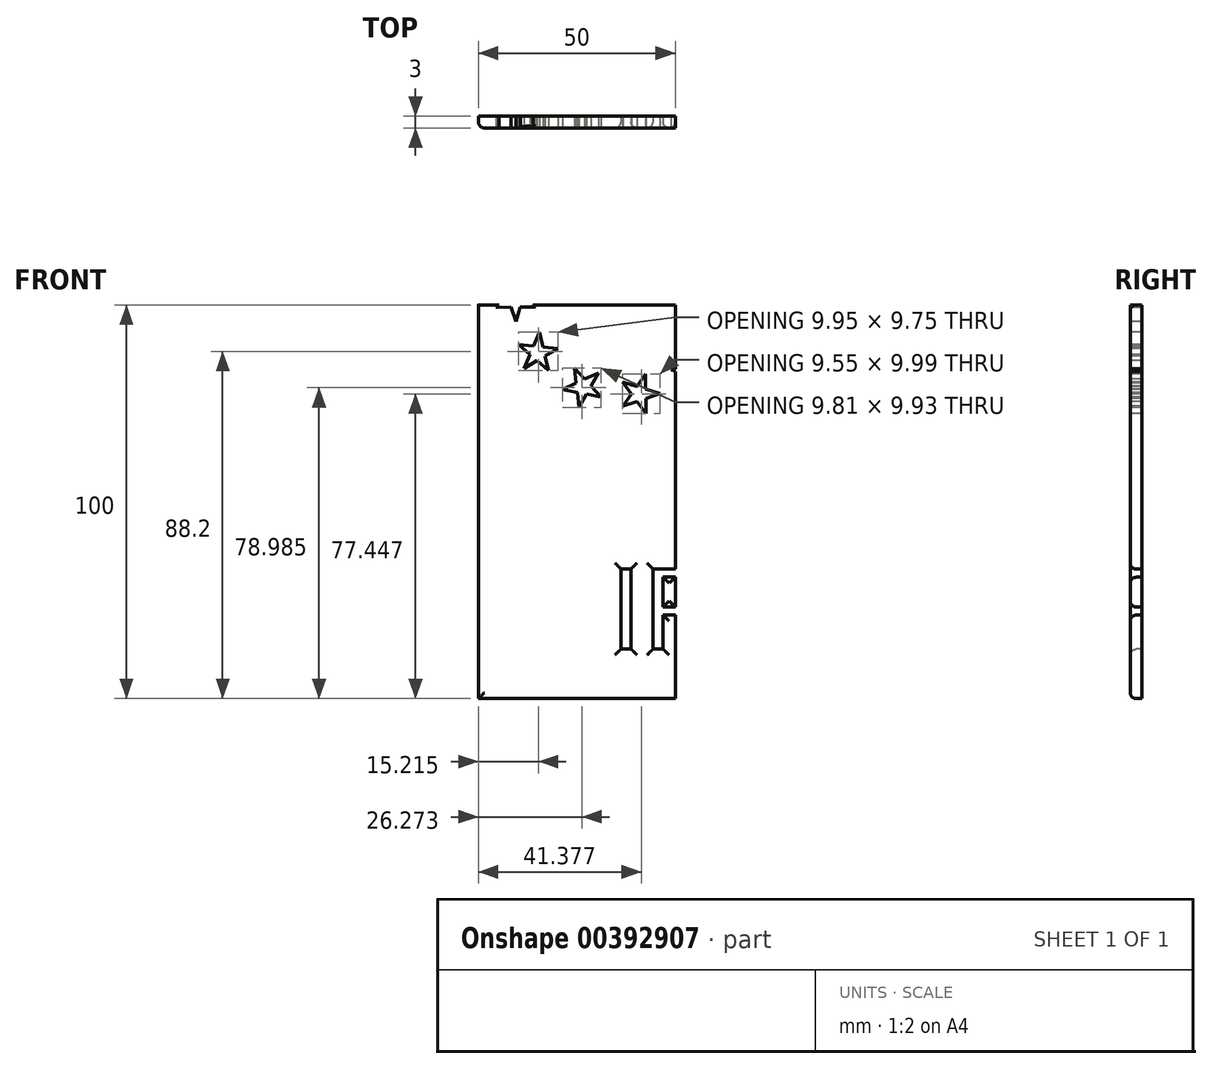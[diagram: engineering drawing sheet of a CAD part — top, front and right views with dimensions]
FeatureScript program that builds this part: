
annotation { "Feature Type Name" : "Feature", "Feature Type Description" : "" }
export const myFeature = defineFeature(function(context is Context, id is Id, definition is map)
    precondition{}
    {
        {
            var Q0;
            Q0=qCreatedBy(makeId("Front.planeOp"),FACE);
            var sketch = newSketch(context, id + "F0", { "sketchPlane" : qUnion([Q0])});
            skLineSegment(sketch, "E0.bottom", {"start": v(0, 0) * mm, "end": v(50, 0) * mm});
            skLineSegment(sketch, "E0.top", {"start": v(0, 100) * mm, "end": v(50, 100) * mm});
            skLineSegment(sketch, "E0.left", {"start": v(0, 0) * mm, "end": v(0, 100) * mm});
            skLineSegment(sketch, "E0.right", {"start": v(50, 0) * mm, "end": v(50, 100) * mm});
            skSolve(sketch);
        }
        {
            var Q0;
            Q0 = qSketchRegion(id + "F0", true);
            extrude(context, id + "F1", {"entities" : qUnion([Q0]), "depth" : 3 * mm});
        }
        {
            var Q0;
            Q0=makeQuery(id+"F1.opExtrude","CAP_FACE",FACE,{"disambiguationData":[OSD([sQuery(id+"F0.wireOp",EDGE,"E0.bottom"),sQuery(id+"F0.wireOp",EDGE,"E0.top"),sQuery(id+"F0.wireOp",EDGE,"E0.left"),sQuery(id+"F0.wireOp",EDGE,"E0.right")])],"isStart":false});
            var sketch = newSketch(context, id + "F2", { "sketchPlane" : qUnion([Q0])});
            skText(sketch, "E1", { "text": "IRL", "fontName": "NotoSansCJKjp-Regular.otf"});
            const initialGuessF2  = {"E1": [0.03342, 0.01257, 1, 0, 0.02]};
            skSetInitialGuess(sketch, initialGuessF2);
            skSolve(sketch);
        }
        {
            var Q0;
            Q0 = qSketchRegion(id + "F2", true);
            extrude(context, id + "F3", {"entities" : qUnion([Q0]), "operationType" : NewBodyOperationType.REMOVE, "oppositeDirection" : true, "depth" : 3 * mm});
        }
        {
            var Q0;
            {var subQ0=sQuery(id+"F0.wireOp",EDGE,"E0.top");var subQ1=sQuery(id+"F0.wireOp",EDGE,"E0.right");var subQ2=sQuery(id+"F0.wireOp",EDGE,"E0.bottom");var subQ3=sQuery(id+"F0.wireOp",EDGE,"E0.left");Q0=makeQuery(id+"F3.boolean.opBoolean","SPLIT",FACE,{"disambiguationData":[TD([makeQuery(id+"F1.opExtrude","SWEPT_FACE",FACE,{"disambiguationData":[OSD([subQ2])]})])],"derivedFrom":makeQuery(id+"F1.opExtrude","CAP_FACE",FACE,{"disambiguationData":[OSD([subQ2,subQ0,subQ3,subQ1])],"isStart":false})});}
            var sketch = newSketch(context, id + "F4", { "sketchPlane" : qUnion([Q0])});
            skPoint(sketch, "E2.0.midPoint", {"position": v(19.37, 90.4) * mm});
            skLineSegment(sketch, "E3", {"start": v(15.55, 93.08) * mm, "end": v(14.04, 89.57) * mm});
            skPoint(sketch, "E4.orphan", {"position": v(16.18, 82.96) * mm});
            skLineSegment(sketch, "E5", {"start": v(15.55, 93.08) * mm, "end": v(16.4, 89.35) * mm});
            skLineSegment(sketch, "E6", {"start": v(17.76, 83.32) * mm, "end": v(14.89, 85.84) * mm});
            skLineSegment(sketch, "E7", {"start": v(10.24, 89.92) * mm, "end": v(14.04, 89.57) * mm});
            skLineSegment(sketch, "E8", {"start": v(20.19, 89) * mm, "end": v(16.92, 87.05) * mm});
            skPoint(sketch, "E9.orphan", {"position": v(14.6, 82.6) * mm});
            skPoint(sketch, "E10.orphan", {"position": v(18.54, 91.8) * mm});
            skPoint(sketch, "E11.orphan", {"position": v(20.2, 89) * mm});
            skLineSegment(sketch, "E12.trimOffspring", {"start": v(16.4, 89.35) * mm, "end": v(20.19, 89) * mm});
            skLineSegment(sketch, "E13.trimOffspring", {"start": v(13.11, 87.4) * mm, "end": v(11.6, 83.89) * mm});
            skLineSegment(sketch, "E14.trimOffspring", {"start": v(13.11, 87.4) * mm, "end": v(10.24, 89.92) * mm});
            skLineSegment(sketch, "E15.trimOffspring", {"start": v(14.89, 85.84) * mm, "end": v(11.6, 83.89) * mm});
            skLineSegment(sketch, "E16.trimOffspring", {"start": v(16.92, 87.05) * mm, "end": v(17.76, 83.32) * mm});
            skLineSegment(sketch, "E17.1.0", {"start": v(28.58, 79.42) * mm, "end": v(31.18, 76.6) * mm});
            skLineSegment(sketch, "E17.1.1", {"start": v(27.43, 77.35) * mm, "end": v(25.56, 74.02) * mm});
            skLineSegment(sketch, "E17.1.2", {"start": v(25.12, 77.81) * mm, "end": v(21.37, 78.56) * mm});
            skLineSegment(sketch, "E17.1.3", {"start": v(25.12, 77.81) * mm, "end": v(25.56, 74.02) * mm});
            skLineSegment(sketch, "E17.1.4", {"start": v(26.98, 81.15) * mm, "end": v(30.44, 82.74) * mm});
            skLineSegment(sketch, "E17.1.5", {"start": v(30.44, 82.74) * mm, "end": v(28.58, 79.42) * mm});
            skLineSegment(sketch, "E17.1.6", {"start": v(21.37, 78.56) * mm, "end": v(24.84, 80.16) * mm});
            skLineSegment(sketch, "E17.1.7", {"start": v(31.18, 76.6) * mm, "end": v(27.43, 77.35) * mm});
            skLineSegment(sketch, "E17.1.8", {"start": v(24.39, 83.95) * mm, "end": v(26.98, 81.15) * mm});
            skLineSegment(sketch, "E17.1.9", {"start": v(24.39, 83.95) * mm, "end": v(24.84, 80.16) * mm});
            skPoint(sketch, "E17.1.10", {"position": v(30.45, 82.75) * mm});
            skPoint(sketch, "E17.1.11", {"position": v(27.61, 84.33) * mm});
            skPoint(sketch, "E17.1.12", {"position": v(28.8, 74.4) * mm});
            skPoint(sketch, "E17.1.13", {"position": v(29.98, 75.5) * mm});
            skPoint(sketch, "E17.1.14", {"position": v(29.03, 83.54) * mm});
            skLineSegment(sketch, "E17.2.0", {"start": v(42.5, 78.63) * mm, "end": v(46.15, 77.5) * mm});
            skLineSegment(sketch, "E17.2.1", {"start": v(42.53, 76.27) * mm, "end": v(42.59, 72.45) * mm});
            skLineSegment(sketch, "E17.2.2", {"start": v(40.3, 75.51) * mm, "end": v(36.68, 74.28) * mm});
            skLineSegment(sketch, "E17.2.3", {"start": v(40.3, 75.51) * mm, "end": v(42.59, 72.45) * mm});
            skLineSegment(sketch, "E17.2.4", {"start": v(40.25, 79.33) * mm, "end": v(42.45, 82.44) * mm});
            skLineSegment(sketch, "E17.2.5", {"start": v(42.45, 82.44) * mm, "end": v(42.5, 78.63) * mm});
            skLineSegment(sketch, "E17.2.6", {"start": v(36.68, 74.28) * mm, "end": v(38.89, 77.4) * mm});
            skLineSegment(sketch, "E17.2.7", {"start": v(46.15, 77.5) * mm, "end": v(42.53, 76.27) * mm});
            skLineSegment(sketch, "E17.2.8", {"start": v(36.6, 80.46) * mm, "end": v(40.25, 79.33) * mm});
            skLineSegment(sketch, "E17.2.9", {"start": v(36.6, 80.46) * mm, "end": v(38.89, 77.4) * mm});
            skPoint(sketch, "E17.2.10", {"position": v(42.45, 82.45) * mm});
            skPoint(sketch, "E17.2.11", {"position": v(39.2, 82.4) * mm});
            skPoint(sketch, "E17.2.12", {"position": v(45.2, 74.4) * mm});
            skPoint(sketch, "E17.2.13", {"position": v(45.67, 75.95) * mm});
            skPoint(sketch, "E17.2.14", {"position": v(40.83, 82.43) * mm});
            skLineSegment(sketch, "E17.3.0", {"start": v(54.95, 84.92) * mm, "end": v(58.68, 85.76) * mm});
            skLineSegment(sketch, "E17.3.1", {"start": v(56.16, 82.89) * mm, "end": v(58.11, 79.6) * mm});
            skLineSegment(sketch, "E17.3.2", {"start": v(54.6, 81.11) * mm, "end": v(52.08, 78.24) * mm});
            skLineSegment(sketch, "E17.3.3", {"start": v(54.6, 81.11) * mm, "end": v(58.11, 79.6) * mm});
            skLineSegment(sketch, "E17.3.4", {"start": v(52.65, 84.4) * mm, "end": v(53, 88.19) * mm});
            skLineSegment(sketch, "E17.3.5", {"start": v(53, 88.19) * mm, "end": v(54.95, 84.92) * mm});
            skLineSegment(sketch, "E17.3.6", {"start": v(52.08, 78.24) * mm, "end": v(52.43, 82.04) * mm});
            skLineSegment(sketch, "E17.3.7", {"start": v(58.68, 85.76) * mm, "end": v(56.16, 82.89) * mm});
            skLineSegment(sketch, "E17.3.8", {"start": v(48.92, 83.55) * mm, "end": v(52.65, 84.4) * mm});
            skLineSegment(sketch, "E17.3.9", {"start": v(48.92, 83.55) * mm, "end": v(52.43, 82.04) * mm});
            skPoint(sketch, "E17.3.10", {"position": v(53, 88.2) * mm});
            skPoint(sketch, "E17.3.11", {"position": v(50.2, 86.54) * mm});
            skPoint(sketch, "E17.3.12", {"position": v(59.4, 82.6) * mm});
            skPoint(sketch, "E17.3.13", {"position": v(59.04, 84.18) * mm});
            skPoint(sketch, "E17.3.14", {"position": v(51.6, 87.37) * mm});
            skLineSegment(sketch, "E17.4.0", {"start": v(62.58, 96.58) * mm, "end": v(65.4, 99.18) * mm});
            skLineSegment(sketch, "E17.4.1", {"start": v(64.65, 95.43) * mm, "end": v(67.98, 93.56) * mm});
            skLineSegment(sketch, "E17.4.2", {"start": v(64.19, 93.12) * mm, "end": v(63.44, 89.37) * mm});
            skLineSegment(sketch, "E17.4.3", {"start": v(64.19, 93.12) * mm, "end": v(67.98, 93.56) * mm});
            skLineSegment(sketch, "E17.4.4", {"start": v(60.85, 94.98) * mm, "end": v(59.26, 98.44) * mm});
            skLineSegment(sketch, "E17.4.5", {"start": v(59.26, 98.44) * mm, "end": v(62.58, 96.58) * mm});
            skLineSegment(sketch, "E17.4.6", {"start": v(63.44, 89.37) * mm, "end": v(61.84, 92.84) * mm});
            skLineSegment(sketch, "E17.4.7", {"start": v(65.4, 99.18) * mm, "end": v(64.65, 95.43) * mm});
            skLineSegment(sketch, "E17.4.8", {"start": v(58.05, 92.39) * mm, "end": v(60.85, 94.98) * mm});
            skLineSegment(sketch, "E17.4.9", {"start": v(58.05, 92.39) * mm, "end": v(61.84, 92.84) * mm});
            skPoint(sketch, "E17.4.10", {"position": v(59.25, 98.45) * mm});
            skPoint(sketch, "E17.4.11", {"position": v(57.67, 95.61) * mm});
            skPoint(sketch, "E17.4.12", {"position": v(67.6, 96.8) * mm});
            skPoint(sketch, "E17.4.13", {"position": v(66.5, 97.98) * mm});
            skPoint(sketch, "E17.4.14", {"position": v(58.46, 97.03) * mm});
            skLineSegment(sketch, "E17.5.0", {"start": v(63.37, 110.5) * mm, "end": v(64.5, 114.15) * mm});
            skLineSegment(sketch, "E17.5.1", {"start": v(65.73, 110.53) * mm, "end": v(69.55, 110.59) * mm});
            skLineSegment(sketch, "E17.5.2", {"start": v(66.49, 108.3) * mm, "end": v(67.72, 104.68) * mm});
            skLineSegment(sketch, "E17.5.3", {"start": v(66.49, 108.3) * mm, "end": v(69.55, 110.59) * mm});
            skLineSegment(sketch, "E17.5.4", {"start": v(62.67, 108.25) * mm, "end": v(59.56, 110.45) * mm});
            skLineSegment(sketch, "E17.5.5", {"start": v(59.56, 110.45) * mm, "end": v(63.37, 110.5) * mm});
            skLineSegment(sketch, "E17.5.6", {"start": v(67.72, 104.68) * mm, "end": v(64.6, 106.89) * mm});
            skLineSegment(sketch, "E17.5.7", {"start": v(64.5, 114.15) * mm, "end": v(65.73, 110.53) * mm});
            skLineSegment(sketch, "E17.5.8", {"start": v(61.54, 104.6) * mm, "end": v(62.67, 108.25) * mm});
            skLineSegment(sketch, "E17.5.9", {"start": v(61.54, 104.6) * mm, "end": v(64.6, 106.89) * mm});
            skPoint(sketch, "E17.5.10", {"position": v(59.55, 110.45) * mm});
            skPoint(sketch, "E17.5.11", {"position": v(59.6, 107.2) * mm});
            skPoint(sketch, "E17.5.12", {"position": v(67.6, 113.2) * mm});
            skPoint(sketch, "E17.5.13", {"position": v(66.05, 113.67) * mm});
            skPoint(sketch, "E17.5.14", {"position": v(59.57, 108.83) * mm});
            skLineSegment(sketch, "E17.6.0", {"start": v(57.08, 122.95) * mm, "end": v(56.24, 126.68) * mm});
            skLineSegment(sketch, "E17.6.1", {"start": v(59.11, 124.16) * mm, "end": v(62.4, 126.11) * mm});
            skLineSegment(sketch, "E17.6.2", {"start": v(60.89, 122.6) * mm, "end": v(63.76, 120.08) * mm});
            skLineSegment(sketch, "E17.6.3", {"start": v(60.89, 122.6) * mm, "end": v(62.4, 126.11) * mm});
            skLineSegment(sketch, "E17.6.4", {"start": v(57.6, 120.65) * mm, "end": v(53.81, 121) * mm});
            skLineSegment(sketch, "E17.6.5", {"start": v(53.81, 121) * mm, "end": v(57.08, 122.95) * mm});
            skLineSegment(sketch, "E17.6.6", {"start": v(63.76, 120.08) * mm, "end": v(59.96, 120.43) * mm});
            skLineSegment(sketch, "E17.6.7", {"start": v(56.24, 126.68) * mm, "end": v(59.11, 124.16) * mm});
            skLineSegment(sketch, "E17.6.8", {"start": v(58.45, 116.92) * mm, "end": v(57.6, 120.65) * mm});
            skLineSegment(sketch, "E17.6.9", {"start": v(58.45, 116.92) * mm, "end": v(59.96, 120.43) * mm});
            skPoint(sketch, "E17.6.10", {"position": v(53.8, 121) * mm});
            skPoint(sketch, "E17.6.11", {"position": v(55.46, 118.2) * mm});
            skPoint(sketch, "E17.6.12", {"position": v(59.4, 127.4) * mm});
            skPoint(sketch, "E17.6.13", {"position": v(57.82, 127.04) * mm});
            skPoint(sketch, "E17.6.14", {"position": v(54.63, 119.6) * mm});
            skLineSegment(sketch, "E17.7.0", {"start": v(45.42, 130.58) * mm, "end": v(42.82, 133.4) * mm});
            skLineSegment(sketch, "E17.7.1", {"start": v(46.57, 132.65) * mm, "end": v(48.44, 135.98) * mm});
            skLineSegment(sketch, "E17.7.2", {"start": v(48.88, 132.19) * mm, "end": v(52.63, 131.44) * mm});
            skLineSegment(sketch, "E17.7.3", {"start": v(48.88, 132.19) * mm, "end": v(48.44, 135.98) * mm});
            skLineSegment(sketch, "E17.7.4", {"start": v(47.02, 128.85) * mm, "end": v(43.56, 127.26) * mm});
            skLineSegment(sketch, "E17.7.5", {"start": v(43.56, 127.26) * mm, "end": v(45.42, 130.58) * mm});
            skLineSegment(sketch, "E17.7.6", {"start": v(52.63, 131.44) * mm, "end": v(49.16, 129.84) * mm});
            skLineSegment(sketch, "E17.7.7", {"start": v(42.82, 133.4) * mm, "end": v(46.57, 132.65) * mm});
            skLineSegment(sketch, "E17.7.8", {"start": v(49.61, 126.05) * mm, "end": v(47.02, 128.85) * mm});
            skLineSegment(sketch, "E17.7.9", {"start": v(49.61, 126.05) * mm, "end": v(49.16, 129.84) * mm});
            skPoint(sketch, "E17.7.10", {"position": v(43.55, 127.25) * mm});
            skPoint(sketch, "E17.7.11", {"position": v(46.39, 125.67) * mm});
            skPoint(sketch, "E17.7.12", {"position": v(45.2, 135.6) * mm});
            skPoint(sketch, "E17.7.13", {"position": v(44.02, 134.5) * mm});
            skPoint(sketch, "E17.7.14", {"position": v(44.97, 126.46) * mm});
            skLineSegment(sketch, "E17.8.0", {"start": v(31.5, 131.37) * mm, "end": v(27.85, 132.5) * mm});
            skLineSegment(sketch, "E17.8.1", {"start": v(31.47, 133.73) * mm, "end": v(31.41, 137.55) * mm});
            skLineSegment(sketch, "E17.8.2", {"start": v(33.7, 134.49) * mm, "end": v(37.32, 135.72) * mm});
            skLineSegment(sketch, "E17.8.3", {"start": v(33.7, 134.49) * mm, "end": v(31.41, 137.55) * mm});
            skLineSegment(sketch, "E17.8.4", {"start": v(33.75, 130.67) * mm, "end": v(31.55, 127.56) * mm});
            skLineSegment(sketch, "E17.8.5", {"start": v(31.55, 127.56) * mm, "end": v(31.5, 131.37) * mm});
            skLineSegment(sketch, "E17.8.6", {"start": v(37.32, 135.72) * mm, "end": v(35.11, 132.6) * mm});
            skLineSegment(sketch, "E17.8.7", {"start": v(27.85, 132.5) * mm, "end": v(31.47, 133.73) * mm});
            skLineSegment(sketch, "E17.8.8", {"start": v(37.4, 129.54) * mm, "end": v(33.75, 130.67) * mm});
            skLineSegment(sketch, "E17.8.9", {"start": v(37.4, 129.54) * mm, "end": v(35.11, 132.6) * mm});
            skPoint(sketch, "E17.8.10", {"position": v(31.55, 127.55) * mm});
            skPoint(sketch, "E17.8.11", {"position": v(34.8, 127.6) * mm});
            skPoint(sketch, "E17.8.12", {"position": v(28.8, 135.6) * mm});
            skPoint(sketch, "E17.8.13", {"position": v(28.33, 134.05) * mm});
            skPoint(sketch, "E17.8.14", {"position": v(33.17, 127.57) * mm});
            skLineSegment(sketch, "E17.9.0", {"start": v(19.05, 125.08) * mm, "end": v(15.32, 124.24) * mm});
            skLineSegment(sketch, "E17.9.1", {"start": v(17.84, 127.11) * mm, "end": v(15.89, 130.4) * mm});
            skLineSegment(sketch, "E17.9.2", {"start": v(19.4, 128.89) * mm, "end": v(21.92, 131.76) * mm});
            skLineSegment(sketch, "E17.9.3", {"start": v(19.4, 128.89) * mm, "end": v(15.89, 130.4) * mm});
            skLineSegment(sketch, "E17.9.4", {"start": v(21.35, 125.6) * mm, "end": v(21, 121.81) * mm});
            skLineSegment(sketch, "E17.9.5", {"start": v(21, 121.81) * mm, "end": v(19.05, 125.08) * mm});
            skLineSegment(sketch, "E17.9.6", {"start": v(21.92, 131.76) * mm, "end": v(21.57, 127.96) * mm});
            skLineSegment(sketch, "E17.9.7", {"start": v(15.32, 124.24) * mm, "end": v(17.84, 127.11) * mm});
            skLineSegment(sketch, "E17.9.8", {"start": v(25.08, 126.45) * mm, "end": v(21.35, 125.6) * mm});
            skLineSegment(sketch, "E17.9.9", {"start": v(25.08, 126.45) * mm, "end": v(21.57, 127.96) * mm});
            skPoint(sketch, "E17.9.10", {"position": v(21, 121.8) * mm});
            skPoint(sketch, "E17.9.11", {"position": v(23.8, 123.46) * mm});
            skPoint(sketch, "E17.9.12", {"position": v(14.6, 127.4) * mm});
            skPoint(sketch, "E17.9.13", {"position": v(14.96, 125.82) * mm});
            skPoint(sketch, "E17.9.14", {"position": v(22.4, 122.63) * mm});
            skLineSegment(sketch, "E17.10.0", {"start": v(11.42, 113.42) * mm, "end": v(8.6, 110.82) * mm});
            skLineSegment(sketch, "E17.10.1", {"start": v(9.35, 114.57) * mm, "end": v(6.02, 116.44) * mm});
            skLineSegment(sketch, "E17.10.2", {"start": v(9.81, 116.88) * mm, "end": v(10.56, 120.63) * mm});
            skLineSegment(sketch, "E17.10.3", {"start": v(9.81, 116.88) * mm, "end": v(6.02, 116.44) * mm});
            skLineSegment(sketch, "E17.10.4", {"start": v(13.15, 115.02) * mm, "end": v(14.74, 111.56) * mm});
            skLineSegment(sketch, "E17.10.5", {"start": v(14.74, 111.56) * mm, "end": v(11.42, 113.42) * mm});
            skLineSegment(sketch, "E17.10.6", {"start": v(10.56, 120.63) * mm, "end": v(12.16, 117.16) * mm});
            skLineSegment(sketch, "E17.10.7", {"start": v(8.6, 110.82) * mm, "end": v(9.35, 114.57) * mm});
            skLineSegment(sketch, "E17.10.8", {"start": v(15.95, 117.61) * mm, "end": v(13.15, 115.02) * mm});
            skLineSegment(sketch, "E17.10.9", {"start": v(15.95, 117.61) * mm, "end": v(12.16, 117.16) * mm});
            skPoint(sketch, "E17.10.10", {"position": v(14.75, 111.55) * mm});
            skPoint(sketch, "E17.10.11", {"position": v(16.33, 114.39) * mm});
            skPoint(sketch, "E17.10.12", {"position": v(6.4, 113.2) * mm});
            skPoint(sketch, "E17.10.13", {"position": v(7.5, 112.02) * mm});
            skPoint(sketch, "E17.10.14", {"position": v(15.54, 112.97) * mm});
            skLineSegment(sketch, "E17.11.0", {"start": v(10.63, 99.5) * mm, "end": v(9.5, 95.85) * mm});
            skLineSegment(sketch, "E17.11.1", {"start": v(8.27, 99.47) * mm, "end": v(4.45, 99.41) * mm});
            skLineSegment(sketch, "E17.11.2", {"start": v(7.51, 101.7) * mm, "end": v(6.28, 105.32) * mm});
            skLineSegment(sketch, "E17.11.3", {"start": v(7.51, 101.7) * mm, "end": v(4.45, 99.41) * mm});
            skLineSegment(sketch, "E17.11.4", {"start": v(11.33, 101.75) * mm, "end": v(14.44, 99.55) * mm});
            skLineSegment(sketch, "E17.11.5", {"start": v(14.44, 99.55) * mm, "end": v(10.63, 99.5) * mm});
            skLineSegment(sketch, "E17.11.6", {"start": v(6.28, 105.32) * mm, "end": v(9.4, 103.11) * mm});
            skLineSegment(sketch, "E17.11.7", {"start": v(9.5, 95.85) * mm, "end": v(8.27, 99.47) * mm});
            skLineSegment(sketch, "E17.11.8", {"start": v(12.46, 105.4) * mm, "end": v(11.33, 101.75) * mm});
            skLineSegment(sketch, "E17.11.9", {"start": v(12.46, 105.4) * mm, "end": v(9.4, 103.11) * mm});
            skPoint(sketch, "E17.11.10", {"position": v(14.45, 99.55) * mm});
            skPoint(sketch, "E17.11.11", {"position": v(14.4, 102.8) * mm});
            skPoint(sketch, "E17.11.12", {"position": v(6.4, 96.8) * mm});
            skPoint(sketch, "E17.11.13", {"position": v(7.95, 96.33) * mm});
            skPoint(sketch, "E17.11.14", {"position": v(14.43, 101.17) * mm});
            skPoint(sketch, "E17.center", {"position": v(37, 105) * mm});
            skSolve(sketch);
        }
        {
            var Q0;
            Q0 = qSketchRegion(id + "F4", true);
            extrude(context, id + "F5", {"entities" : qUnion([Q0]), "operationType" : NewBodyOperationType.REMOVE, "oppositeDirection" : true, "depth" : 3 * mm});
        }
        {
            var Q0;
            Q0=makeQuery(id+"F1.opExtrude","CAP_EDGE",EDGE,{"disambiguationData":[OSD([sQuery(id+"F0.wireOp",EDGE,"E0.left")])],"isStart":false});
            var Q1;
            {var subQ0=sQuery(id+"F0.wireOp",EDGE,"E0.right");var subQ1=sQuery(id+"F0.wireOp",EDGE,"E0.top");Q1=makeQuery(id+"F5.boolean.opBoolean","SPLIT",EDGE,{"disambiguationData":[TD([makeQuery(id+"F1.opExtrude","SWEPT_FACE",FACE,{"disambiguationData":[OSD([subQ0])]})])],"derivedFrom":makeQuery(id+"F1.opExtrude","CAP_EDGE",EDGE,{"disambiguationData":[OSD([subQ1])],"isStart":false})});}
            var Q2;
            {var subQ0=sQuery(id+"F0.wireOp",EDGE,"E0.bottom");var subQ1=sQuery(id+"F0.wireOp",EDGE,"E0.right");Q2=makeQuery(id+"F5.boolean.opBoolean","SPLIT",EDGE,{"disambiguationData":[TD([makeQuery(id+"F1.opExtrude","SWEPT_FACE",FACE,{"disambiguationData":[OSD([subQ0])]})])],"derivedFrom":makeQuery(id+"F1.opExtrude","CAP_EDGE",EDGE,{"disambiguationData":[OSD([subQ1])],"isStart":false})});}
            var Q3;
            Q3=makeQuery(id+"F1.opExtrude","CAP_EDGE",EDGE,{"disambiguationData":[OSD([sQuery(id+"F0.wireOp",EDGE,"E0.bottom")])],"isStart":false});
            var Q4;
            Q4=makeQuery(id+"F3.boolean.opBoolean","COPY",EDGE,{"derivedFrom":makeQuery(id+"F3.opExtrude","CAP_EDGE",EDGE,{"disambiguationData":[OSD([sQuery(id+"F2.wireOp",EDGE,"E1.sketch_text.stroke-3")])],"isStart":true})});
            var Q5;
            Q5=makeQuery(id+"F3.boolean.opBoolean","COPY",EDGE,{"derivedFrom":makeQuery(id+"F3.opExtrude","CAP_EDGE",EDGE,{"disambiguationData":[OSD([sQuery(id+"F2.wireOp",EDGE,"E1.sketch_text.stroke-2")])],"isStart":true})});
            var Q6;
            Q6=makeQuery(id+"F3.boolean.opBoolean","COPY",EDGE,{"derivedFrom":makeQuery(id+"F3.opExtrude","CAP_EDGE",EDGE,{"disambiguationData":[OSD([sQuery(id+"F2.wireOp",EDGE,"E1.sketch_text.stroke-1")])],"isStart":true})});
            var Q7;
            Q7=makeQuery(id+"F3.boolean.opBoolean","COPY",EDGE,{"derivedFrom":makeQuery(id+"F3.opExtrude","CAP_EDGE",EDGE,{"disambiguationData":[OSD([sQuery(id+"F2.wireOp",EDGE,"E1.sketch_text.stroke-0")])],"isStart":true})});
            var Q8;
            Q8=makeQuery(id+"F3.boolean.opBoolean","COPY",EDGE,{"derivedFrom":makeQuery(id+"F3.opExtrude","CAP_EDGE",EDGE,{"disambiguationData":[OSD([sQuery(id+"F2.wireOp",EDGE,"E1.sketch_text.stroke-13")])],"isStart":true})});
            var Q9;
            Q9=makeQuery(id+"F3.boolean.opBoolean","COPY",EDGE,{"derivedFrom":makeQuery(id+"F3.opExtrude","CAP_EDGE",EDGE,{"disambiguationData":[OSD([sQuery(id+"F2.wireOp",EDGE,"E1.sketch_text.stroke-12")])],"isStart":true})});
            var Q10;
            Q10=makeQuery(id+"F3.boolean.opBoolean","SPLIT",FACE,{"disambiguationData":[TD([makeQuery(id+"F3.opExtrude","SWEPT_FACE",FACE,{"disambiguationData":[OSD([sQuery(id+"F2.wireOp",EDGE,"E1.sketch_text.stroke-4")])]})])],"derivedFrom":makeQuery(id+"F1.opExtrude","CAP_FACE",FACE,{"disambiguationData":[OSD([sQuery(id+"F0.wireOp",EDGE,"E0.bottom"),sQuery(id+"F0.wireOp",EDGE,"E0.top"),sQuery(id+"F0.wireOp",EDGE,"E0.left"),sQuery(id+"F0.wireOp",EDGE,"E0.right")])],"isStart":false})});
            var Q11;
            Q11=makeQuery(id+"F3.boolean.opBoolean","COPY",EDGE,{"derivedFrom":makeQuery(id+"F3.opExtrude","CAP_EDGE",EDGE,{"disambiguationData":[OSD([sQuery(id+"F2.wireOp",EDGE,"E1.sketch_text.stroke-9")])],"isStart":true})});
            var Q12;
            Q12=makeQuery(id+"F3.boolean.opBoolean","COPY",EDGE,{"derivedFrom":makeQuery(id+"F3.opExtrude","CAP_EDGE",EDGE,{"disambiguationData":[OSD([sQuery(id+"F2.wireOp",EDGE,"E1.sketch_text.stroke-18")])],"isStart":true})});
            var Q13;
            Q13=makeQuery(id+"F3.boolean.opBoolean","COPY",EDGE,{"derivedFrom":makeQuery(id+"F3.opExtrude","CAP_EDGE",EDGE,{"disambiguationData":[OSD([sQuery(id+"F2.wireOp",EDGE,"E1.sketch_text.stroke-17")])],"isStart":true})});
            var Q14;
            Q14=makeQuery(id+"F3.boolean.opBoolean","COPY",EDGE,{"derivedFrom":makeQuery(id+"F3.opExtrude","CAP_EDGE",EDGE,{"disambiguationData":[OSD([sQuery(id+"F2.wireOp",EDGE,"E1.sketch_text.stroke-15")])],"isStart":true})});
            var Q15;
            Q15=makeQuery(id+"F3.boolean.opBoolean","COPY",EDGE,{"derivedFrom":makeQuery(id+"F3.opExtrude","CAP_EDGE",EDGE,{"disambiguationData":[OSD([sQuery(id+"F2.wireOp",EDGE,"E1.sketch_text.stroke-16")])],"isStart":true})});
            var Q16;
            Q16=makeQuery(id+"F3.boolean.opBoolean","COPY",EDGE,{"derivedFrom":makeQuery(id+"F3.opExtrude","CAP_EDGE",EDGE,{"disambiguationData":[OSD([sQuery(id+"F2.wireOp",EDGE,"E1.sketch_text.stroke-14")])],"isStart":true})});
            var Q17;
            Q17=makeQuery(id+"F3.boolean.opBoolean","COPY",EDGE,{"derivedFrom":makeQuery(id+"F3.opExtrude","CAP_EDGE",EDGE,{"disambiguationData":[OSD([sQuery(id+"F2.wireOp",EDGE,"E1.sketch_text.stroke-23")])],"isStart":true})});
            var Q18;
            Q18=makeQuery(id+"F3.boolean.opBoolean","COPY",EDGE,{"derivedFrom":makeQuery(id+"F3.opExtrude","CAP_EDGE",EDGE,{"disambiguationData":[OSD([sQuery(id+"F2.wireOp",EDGE,"E1.sketch_text.stroke-24")])],"isStart":true})});
            var Q19;
            Q19=makeQuery(id+"F3.boolean.opBoolean","COPY",EDGE,{"derivedFrom":makeQuery(id+"F3.opExtrude","CAP_EDGE",EDGE,{"disambiguationData":[OSD([sQuery(id+"F2.wireOp",EDGE,"E1.sketch_text.stroke-22")])],"isStart":true})});
            var Q20;
            Q20=makeQuery(id+"F3.boolean.opBoolean","COPY",EDGE,{"derivedFrom":makeQuery(id+"F3.opExtrude","CAP_EDGE",EDGE,{"disambiguationData":[OSD([sQuery(id+"F2.wireOp",EDGE,"E1.sketch_text.stroke-21")])],"isStart":true})});
            var Q21;
            Q21=makeQuery(id+"F3.boolean.opBoolean","COPY",EDGE,{"derivedFrom":makeQuery(id+"F3.opExtrude","CAP_EDGE",EDGE,{"disambiguationData":[OSD([sQuery(id+"F2.wireOp",EDGE,"E1.sketch_text.stroke-19")])],"isStart":true})});
            fillet(context, id + "F6", {"entities" : qUnion([Q0, Q1, Q2, Q3, Q4, Q5, Q6, Q7, Q8, Q9, Q10, Q11, Q12, Q13, Q14, Q15, Q16, Q17, Q18, Q19, Q20, Q21]), "radius" : 1.5 * mm, "tangentPropagation" : true, "allowEdgeOverflow" : false});
        }
    });
